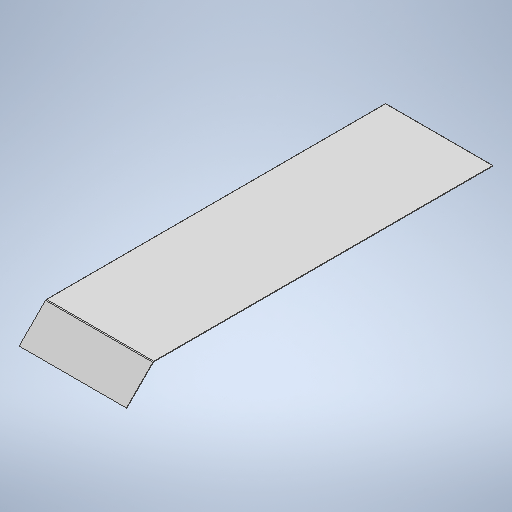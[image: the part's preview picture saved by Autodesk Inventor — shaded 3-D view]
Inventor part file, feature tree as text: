
AUTODESK INVENTOR PART (.ipt)
format: ipt  version: 2025 (Build 290162010, 162A)  size: 335,872 bytes
history: native  units: mm
features: sheet_metal_op x4, other x4, sketch x3
ambient origin geometry x8: Origin, YZ Plane, XZ Plane, XY Plane, X Axis, Y Axis, Z Axis, Center Point
bodies: Solid1 (feature_tree)
feature tree (11):
  sheet_metal_op  "Face1"
  sheet_metal_op  "Flange2"
  other  "Mark1"
  sketch  "Sketch1"  dims[d0=600.0mm]
  other  "Plate1"
  sketch  "Sketch3"  dims[d1=1900.0mm]
  other  "Plate3"
  sheet_metal_op  "Bend2"
  sheet_metal_op  "Corner2"
  sketch  "Sketch5"  dims[d2=3.0mm d13=3.0mm d14=1.5mm d15=6.0mm d16=5.0mm d17=212.0mm d18=45.0deg d19=5.0mm d20=12.0mm d21=3.0mm d22=5.0mm d23=200.0mm d24=11.661mm d25=25.0mm d26=25.0mm]
  other  "Definition1"
